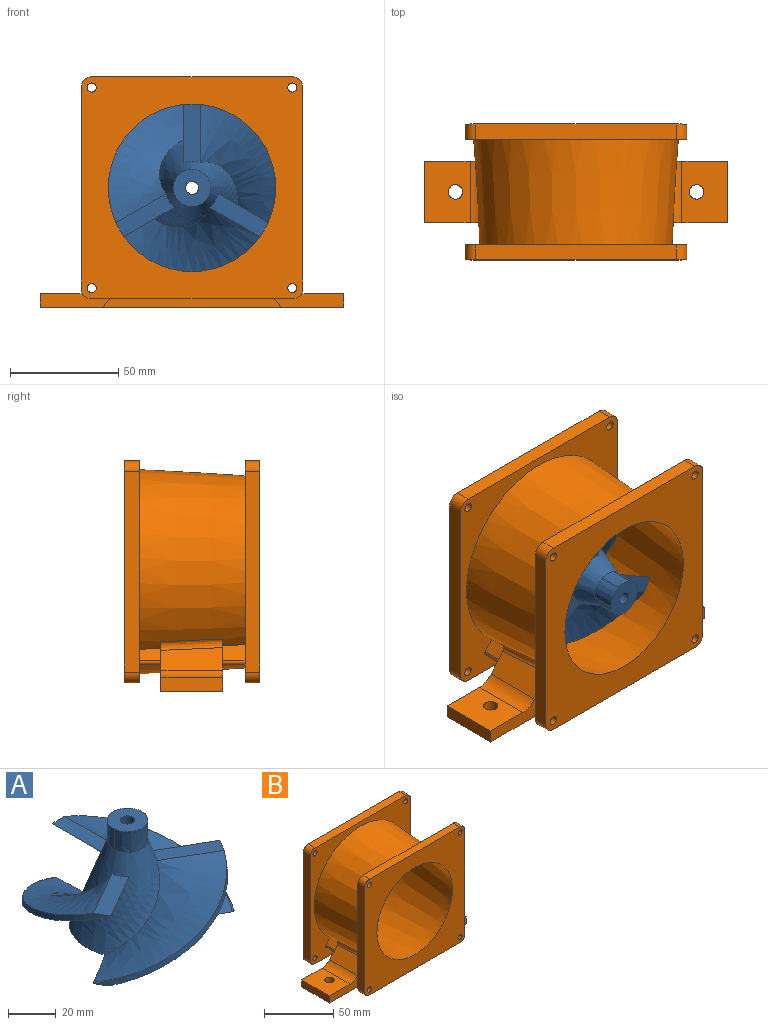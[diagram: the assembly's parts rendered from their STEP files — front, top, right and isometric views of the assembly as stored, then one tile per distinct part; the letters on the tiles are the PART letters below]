
ASSEMBLY  parts=2 mates=1
PART A: 32 faces, bbox 92.7x93.1x58.5 mm
  f0: plane 29.21x21.22mm, normal (0,0,1), area 218.3mm2, adj f4,f13,f17,f31
  f1: plane 29.23x21.2mm, normal (0,0,1), area 218.3mm2, adj f4,f18,f22,f30
  f2: plane 29.6x7.52mm, normal (0,0,1), area 218.3mm2, adj f4,f23,f27,f29
  f3: plane 82.76x72.88mm, normal (0,0,-1), area 2338.9mm2, adj f4,f5,f13,f14,f15,f16,f17,f18
  f4: bspline ~48.97x48.96mm, area 3936mm2, adj f0,f1,f2,f3,f5,f7,f8,f9
  f5: bspline ~6.68x4.23mm, area 14.8mm2, adj f3,f4,f13
  f6: plane 17.27x17.2mm, normal (0,0,1), area 204.2mm2, adj f7,f8,f9,f10,f11,f12,f28
  f7: extruded ~10.6x8.36mm, area 108.6mm2, adj f4,f6,f8,f12
  f8: extruded ~10.6x7.5mm, area 82.3mm2, adj f4,f6,f7,f9
  f9: extruded ~10.6x8.36mm, area 108.6mm2, adj f4,f6,f8,f10
  f10: extruded ~10.6x6.5mm, area 82.3mm2, adj f4,f6,f9,f11
  f11: extruded ~10.6x9.66mm, area 108.6mm2, adj f4,f6,f10,f12
  f12: extruded ~10.6x6.5mm, area 82.3mm2, adj f4,f6,f7,f11
  f13: bspline ~71.5x53.82mm, area 1816.8mm2, adj f0,f3,f4,f5,f14,f31
  f14: bspline ~35.08x12.5mm, area 9.9mm2, adj f3,f13,f15,f31
  f15: bspline ~6.03x0.19mm, area 0.8mm2, adj f3,f14,f16,f31
  f16: bspline ~19.9x6.71mm, area 9.9mm2, adj f3,f15,f17,f31
  f17: bspline ~64.51x60.57mm, area 1816.6mm2, adj f0,f3,f4,f16,f31
  f18: bspline ~83x44.72mm, area 1817.4mm2, adj f1,f3,f4,f19,f30
  f19: bspline ~26.76x24.37mm, area 9.9mm2, adj f3,f18,f20,f30
  f20: bspline ~5.14x3.14mm, area 0.8mm2, adj f3,f19,f21,f30
  f21: bspline ~16.09x12.4mm, area 9.9mm2, adj f3,f20,f22,f30
  f22: bspline ~77.22x42.12mm, area 1818mm2, adj f1,f3,f4,f21,f30
  f23: bspline ~74.6x49.31mm, area 1817.4mm2, adj f2,f3,f4,f24,f29
  f24: bspline ~34.16x12.5mm, area 9.9mm2, adj f3,f23,f25,f29
  f25: bspline ~5.29x2.88mm, area 0.8mm2, adj f3,f24,f26,f29
  f26: bspline ~18.49x7.97mm, area 9.9mm2, adj f3,f25,f27,f29
  f27: bspline ~79.16x42.74mm, area 1818mm2, adj f2,f3,f4,f26,f29
  f28: cylinder r=2.99mm len=53.6mm, axis (0,0,1), area 1007mm2, adj f3,f6
  f29: cone r=45.92mm half-angle=8deg, axis (0,0,-1), area 243.2mm2, adj f2,f23,f24,f25,f26,f27
  f30: cone r=45.92mm half-angle=8deg, axis (0,0,-1), area 243.2mm2, adj f1,f18,f19,f20,f21,f22
  f31: cone r=45.92mm half-angle=8deg, axis (0,0,-1), area 243.2mm2, adj f0,f13,f14,f15,f16,f17
PART B: 67 faces, bbox 140.4x126.9x106.6 mm
  f0: plane 17.59x14.76mm, normal (-0.77,0,-0.64), area 265.9mm2, adj f2,f39,f40,f59
  f1: plane 17.59x14.76mm, normal (0.77,0,-0.64), area 265.9mm2, adj f2,f6,f39,f59
  f2: cone r=44.18mm half-angle=3.3deg, axis (0,1,0), area 1294.9mm2, adj f0,f1,f6,f29,f40,f49,f55,f59
  f3: plane 102.7x102.7mm, normal (0,1,0), area 4176.1mm2, adj f4,f5,f8,f9,f10,f11,f12,f13
  f4: cone r=44.18mm half-angle=3.3deg, axis (0,1,0), area 10679.8mm2, adj f3,f6,f7,f29,f40,f41,f46,f50
  f5: cone r=44.18mm half-angle=3.3deg, axis (0,1,0), area 1272mm2, adj f3,f7,f35,f41,f45,f48,f54,f60
  f6: plane 43.12x22.97mm, normal (0,1,0), area 281mm2, adj f1,f2,f4,f39,f42,f43,f44,f49
  f7: plane 44.16x24.21mm, normal (0,-1,0), area 286.9mm2, adj f4,f5,f39,f42,f43,f44,f45,f46
  f8: plane 92.7x6.85mm, normal (-1,0,0), area 635mm2, adj f3,f16,f17,f20
  f9: plane 92.7x6.85mm, normal (0,0,-1), area 635mm2, adj f3,f16,f17,f18
  f10: plane 92.7x6.85mm, normal (1,0,0), area 635mm2, adj f3,f16,f18,f19
  f11: cylinder r=2.1mm len=6.85mm, axis (0,-1,0), area 90.4mm2, adj f3,f16
  f12: plane 92.7x6.85mm, normal (0,0,1), area 635mm2, adj f3,f16,f19,f20
  f13: cylinder r=2.1mm len=6.85mm, axis (0,-1,0), area 90.4mm2, adj f3,f16
  f14: cylinder r=2.1mm len=6.85mm, axis (0,-1,0), area 90.4mm2, adj f3,f16
  f15: cylinder r=2.1mm len=6.85mm, axis (0,-1,0), area 90.4mm2, adj f3,f16
  f16: plane 102.7x102.7mm, normal (0,-1,0), area 5753.1mm2, adj f8,f9,f10,f11,f12,f13,f14,f15
  f17: cylinder r=5mm len=6.85mm, axis (0,-1,0), area 53.8mm2, adj f3,f8,f9,f16
  f18: cylinder r=5mm len=6.85mm, axis (0,1,0), area 53.8mm2, adj f3,f9,f10,f16
  f19: cylinder r=5mm len=6.85mm, axis (0,-1,0), area 53.8mm2, adj f3,f10,f12,f16
  f20: cylinder r=5mm len=6.85mm, axis (0,1,0), area 53.8mm2, adj f3,f8,f12,f16
  f21: plane 92.7x7mm, normal (1,0,0), area 648.9mm2, adj f29,f30,f31,f34
  f22: plane 92.7x7mm, normal (0,0,-1), area 648.9mm2, adj f29,f30,f31,f32
  f23: plane 92.7x7mm, normal (-1,0,0), area 648.9mm2, adj f29,f30,f32,f33
  f24: cylinder r=2.1mm len=7mm, axis (0,1,0), area 92.4mm2, adj f29,f30
  f25: cylinder r=2.1mm len=7mm, axis (0,1,0), area 92.4mm2, adj f29,f30
  f26: cylinder r=2.1mm len=7mm, axis (0,1,0), area 92.4mm2, adj f29,f30
  f27: cylinder r=2.1mm len=7mm, axis (0,1,0), area 92.4mm2, adj f29,f30
  f28: plane 92.7x7mm, normal (0,0,1), area 648.9mm2, adj f29,f30,f33,f34
  f29: plane 102.7x102.7mm, normal (0,-1,0), area 3387.2mm2, adj f2,f4,f21,f22,f23,f24,f25,f26
  f30: plane 102.7x102.7mm, normal (0,1,0), area 3352.3mm2, adj f21,f22,f23,f24,f25,f26,f27,f28
  f31: cylinder r=5mm len=7mm, axis (0,1,0), area 55mm2, adj f21,f22,f29,f30
  f32: cylinder r=5mm len=7mm, axis (0,-1,0), area 55mm2, adj f22,f23,f29,f30
  f33: cylinder r=5mm len=7mm, axis (0,1,0), area 55mm2, adj f23,f28,f29,f30
  f34: cylinder r=5mm len=7mm, axis (0,-1,0), area 55mm2, adj f21,f28,f29,f30
  f35: plane 18.33x15.38mm, normal (-0.77,0,-0.64), area 277.1mm2, adj f5,f39,f41,f60
  f36: plane 28.5x10.36mm, normal (0.77,0,0.64), area 362.1mm2, adj f40,f41,f64,f65
  f37: plane 28.5x21.15mm, normal (0,0,1), area 567.4mm2, adj f38,f40,f41,f62,f65
  f38: plane 28.5x6.2mm, normal (1,0,0), area 176.7mm2, adj f37,f39,f40,f41
  f39: plane 140.3x28.5mm, normal (0,0,-1), area 1979.9mm2, adj f0,f1,f6,f7,f35,f38,f40,f41
  f40: plane 43.12x22.97mm, normal (0,1,0), area 281mm2, adj f0,f2,f4,f36,f37,f38,f39,f55
  f41: plane 44.17x24.22mm, normal (0,-1,0), area 286.9mm2, adj f4,f5,f35,f36,f37,f38,f39,f52
  f42: plane 28.5x6.2mm, normal (-1,0,0), area 176.7mm2, adj f6,f7,f39,f43
  f43: plane 28.5x21.15mm, normal (0,0,1), area 567.4mm2, adj f6,f7,f42,f61,f66
  f44: plane 28.5x10.36mm, normal (-0.77,0,0.64), area 362.1mm2, adj f6,f7,f63,f66
  f45: plane 18.33x15.38mm, normal (0.77,0,-0.64), area 277.1mm2, adj f5,f7,f39,f60
  f46: plane 10.4x7.12mm, normal (-0.77,0,0.64), area 93.6mm2, adj f3,f4,f7,f47
  f47: cylinder r=1.3mm len=10.4mm, axis (0,1,0), area 42.5mm2, adj f3,f7,f46,f48
  f48: plane 10.4x7.15mm, normal (0.77,0,-0.64), area 93.9mm2, adj f3,f5,f7,f47
  f49: plane 10x5.45mm, normal (0.77,0,-0.64), area 68.3mm2, adj f2,f6,f29,f51
  f50: plane 10x5.42mm, normal (-0.77,0,0.64), area 67.9mm2, adj f4,f6,f29,f51
  f51: cylinder r=1.3mm len=10mm, axis (0,1,0), area 40.8mm2, adj f6,f29,f49,f50
  f52: plane 10.4x7.12mm, normal (0.77,0,0.64), area 93.6mm2, adj f3,f4,f41,f53
  f53: cylinder r=1.3mm len=10.4mm, axis (0,1,0), area 42.5mm2, adj f3,f41,f52,f54
  f54: plane 10.4x7.15mm, normal (-0.77,0,-0.64), area 93.9mm2, adj f3,f5,f41,f53
  f55: plane 10x5.45mm, normal (-0.77,0,-0.64), area 68.3mm2, adj f2,f29,f40,f57
  f56: plane 10x5.42mm, normal (0.77,0,0.64), area 67.9mm2, adj f4,f29,f40,f57
  f57: cylinder r=1.3mm len=10mm, axis (0,1,0), area 40.8mm2, adj f29,f40,f55,f56
  f58: cone r=38.75mm half-angle=8deg, axis (0,1,0), area 17191.1mm2, adj f16,f30
  f59: plane 82.9x17.59mm, normal (0,1,0), area 890mm2, adj f0,f1,f2,f39
  f60: plane 82.9x17.81mm, normal (0,-1,0), area 906.1mm2, adj f5,f35,f39,f45
  f61: cylinder r=3.35mm len=6.7mm, axis (0,0,-1), area 130.5mm2, adj f39,f43
  f62: cylinder r=3.35mm len=6.7mm, axis (0,0,-1), area 130.5mm2, adj f37,f39
  f63: bspline ~123.53x9.39mm, area 125mm2, adj f4,f6,f7,f44
  f64: bspline ~126.85x9.53mm, area 124.9mm2, adj f4,f36,f40,f41
  f65: cylinder r=10mm len=28.5mm, axis (0,1,0), area 248.7mm2, adj f36,f37,f40,f41
  f66: cylinder r=10mm len=28.5mm, axis (0,1,0), area 248.7mm2, adj f6,f7,f43,f44
PLACE A rot(axis=(1,0,0),90deg) t=(8.62,-5.6,5.18)mm
PLACE B t=(8.62,-59.2,5.18)mm
MATE revolute A.f28 <-> B.f2  axis (0,-1,0) through (8.62,-59.2,5.18)mm
